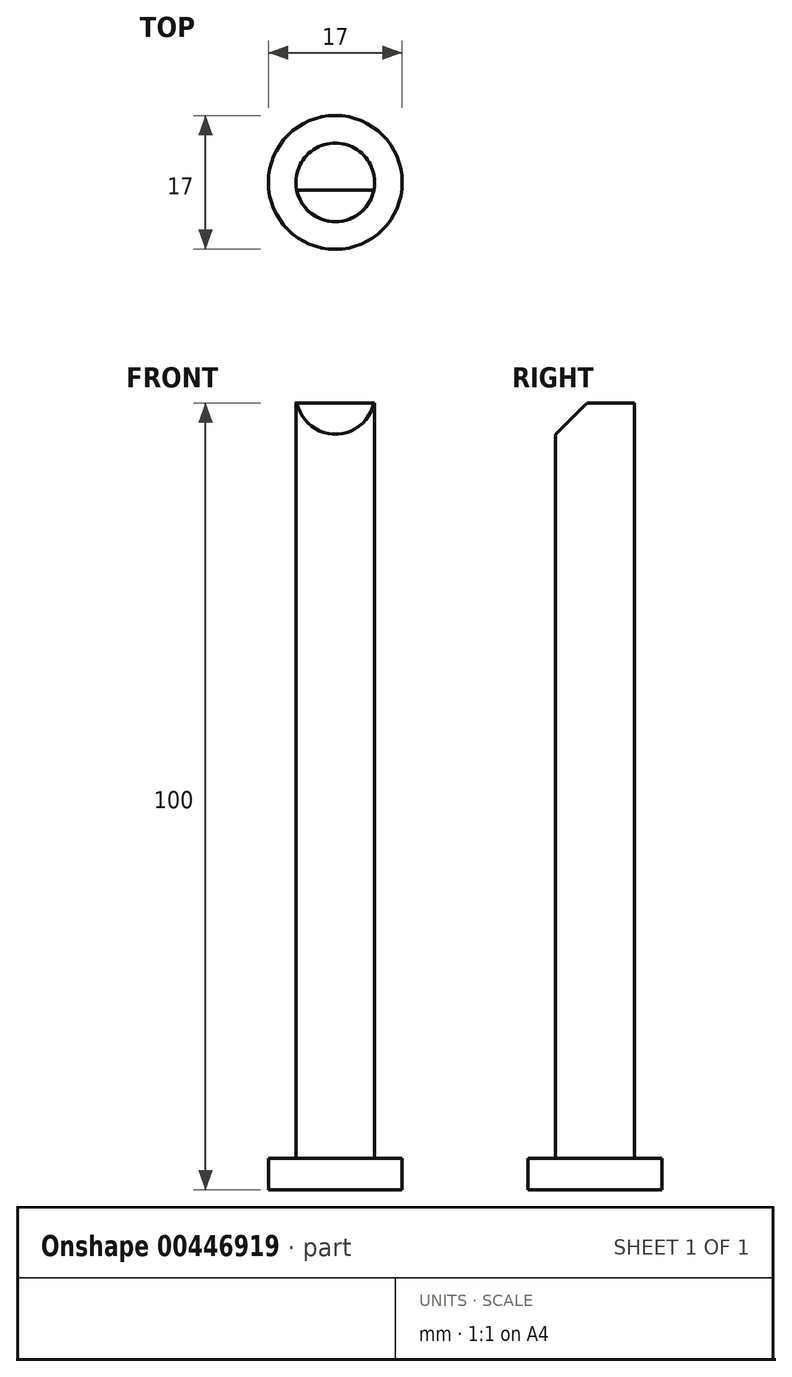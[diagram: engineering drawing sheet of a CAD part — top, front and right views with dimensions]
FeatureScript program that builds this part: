
annotation { "Feature Type Name" : "Feature", "Feature Type Description" : "" }
export const myFeature = defineFeature(function(context is Context, id is Id, definition is map)
    precondition{}
    {
        {
            var Q0;
            Q0=qCreatedBy(makeId("Top.planeOp"),FACE);
            var sketch = newSketch(context, id + "F0", { "sketchPlane" : qUnion([Q0])});
            skCircle(sketch, "E0", {"center": v(0, 0) * mm, "radius": 8.5 * mm});
            skSolve(sketch);
        }
        {
            var Q0;
            Q0=qSketchRegion(id+"F0",true);
            extrude(context, id + "F1", {"entities" : qUnion([Q0]), "depth" : 4 * mm});
        }
        {
            var Q0;
            Q0=qCreatedBy(makeId("Top.planeOp"),FACE);
            var sketch = newSketch(context, id + "F2", { "sketchPlane" : qUnion([Q0])});
            skCircle(sketch, "E1", {"center": v(0, 0) * mm, "radius": 5 * mm});
            skSolve(sketch);
        }
        {
            var Q0;
            Q0=qSketchRegion(id+"F2",true);
            extrude(context, id + "F3", {"entities" : qUnion([Q0]), "operationType" : NewBodyOperationType.ADD, "depth" : 100 * mm});
        }
        {
            var Q0;
            Q0=qCreatedBy(makeId("Right.planeOp"),FACE);
            var sketch = newSketch(context, id + "F4", { "sketchPlane" : qUnion([Q0])});
            skLineSegment(sketch, "E2", {"start": v(-5, 101) * mm, "end": v(-5, 96) * mm});
            skLineSegment(sketch, "E3", {"start": v(-5, 96) * mm, "end": v(0, 101) * mm});
            skLineSegment(sketch, "E4", {"start": v(0, 101) * mm, "end": v(-5, 101) * mm});
            skSolve(sketch);
        }
        {
            var Q0;
            Q0=qSketchRegion(id+"F4",true);
            extrude(context, id + "F5", {"entities" : qUnion([Q0]), "operationType" : NewBodyOperationType.REMOVE, "depth" : 25 * mm, "hasSecondDirection" : true, "secondDirectionOppositeDirection" : true, "secondDirectionDepth" : 25 * mm});
        }
    });
